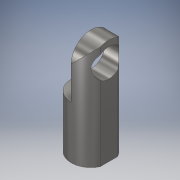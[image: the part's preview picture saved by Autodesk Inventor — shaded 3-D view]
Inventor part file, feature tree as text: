
AUTODESK INVENTOR PART (.ipt)
format: ipt  version: 2018 (Build 220112000, 112)  size: 146,944 bytes
history: native  units: in
note: dims shown in document units (in); Inventor stores cm internally (conversion verified against a paired STEP export)
features: sketch x6, extrude x4, hole x2
ambient origin geometry x8: Origin, YZ Plane, XZ Plane, XY Plane, X Axis, Y Axis, Z Axis, Center Point
bodies: Solid1 (feature_tree)
feature tree (12):
  extrude  "Extrusion1"  Depth=0.5in TaperAngle=0.0deg
  hole  "Hole1"  [1 undecoded]
  extrude  "Extrusion2"  Depth=0.5in TaperAngle=0.0deg
  extrude  "Extrusion3"  Depth=1.0in TaperAngle=0.0deg
  hole  "Hole2"  [1 undecoded]
  extrude  "Extrusion4"  [1 undecoded]
  sketch  "Sketch1"  dims[d0=0.375in d1=0.5in d2=0.0in]
  sketch  "Sketch2"  dims[d3=0.196in d4=0.5in d5=0.375in d6=0.25in d7=0.5635in d8=0.75in d9=0.8108in d10=0.375in]
  sketch  "Sketch3"  dims[d11=0.5in d12=0.0in d13=0.5in d14=0.0in]
  sketch  "Sketch4"  dims[d15=0.266in d16=0.5in d17=0.507in d18=0.25in d19=0.5635in d20=0.75in d21=0.8108in d22=1.0in d23=0.0in]
  sketch  "Sketch5"
  sketch  "Sketch6"
note: 3 required parameter values undecoded (feature->parameter linkage not recoverable at this tier; creation-order binding heuristic only, values carry confidence <= 0.55)
